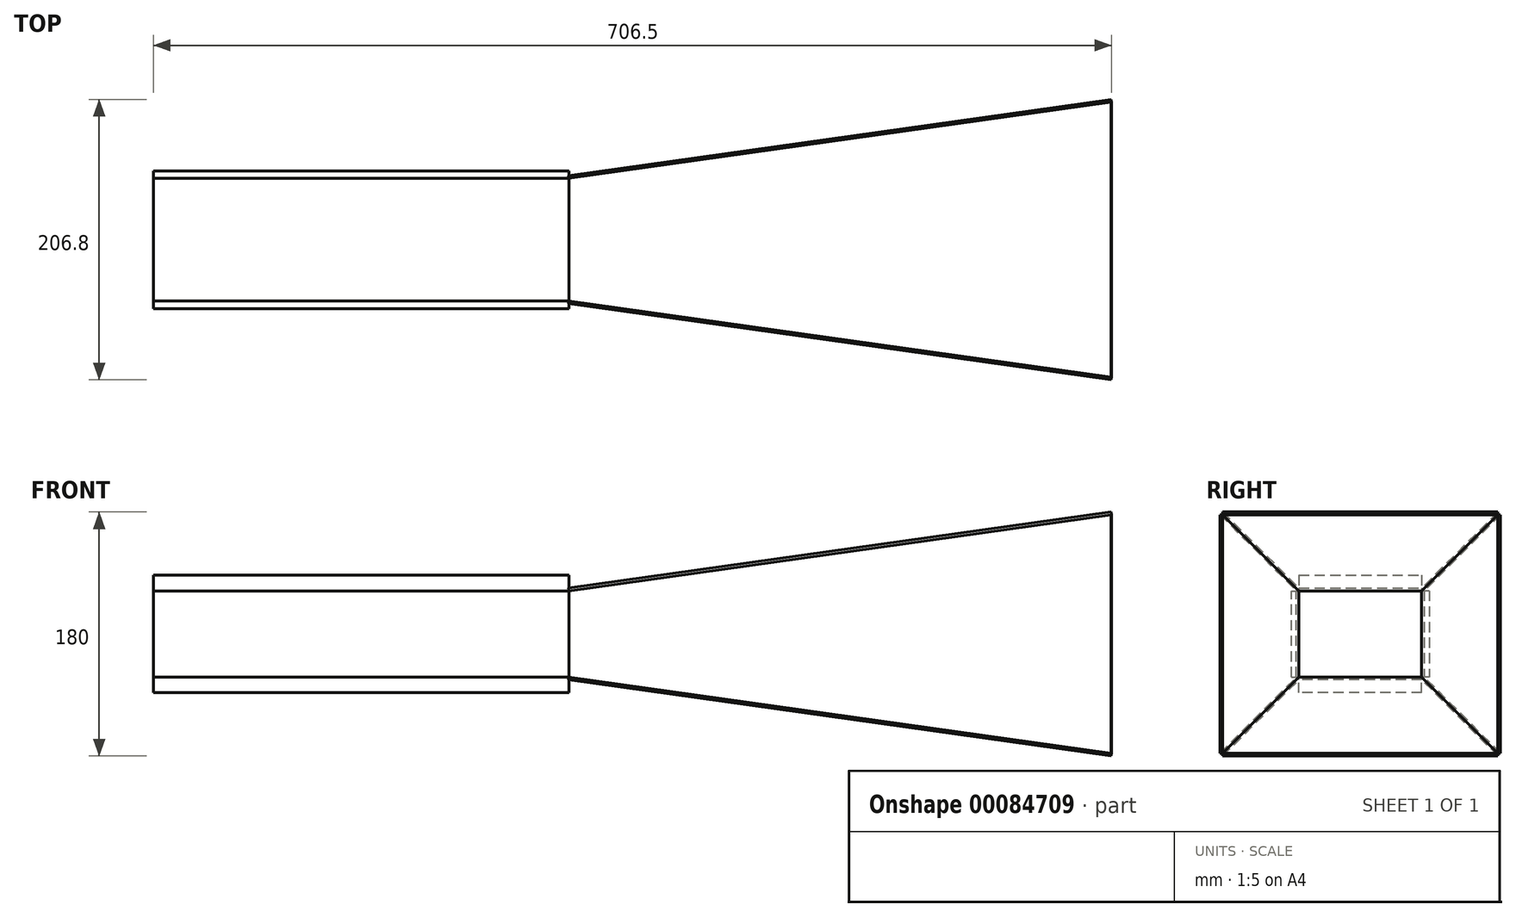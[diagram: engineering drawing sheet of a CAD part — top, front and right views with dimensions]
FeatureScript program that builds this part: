
annotation { "Feature Type Name" : "Feature", "Feature Type Description" : "" }
export const myFeature = defineFeature(function(context is Context, id is Id, definition is map)
    precondition{}
    {
        {
            var Q0;
            Q0=qCreatedBy(makeId("Right.planeOp"),FACE);
            var sketch = newSketch(context, id + "F0", { "sketchPlane" : qUnion([Q0])});
            skLineSegment(sketch, "E0", {"start": v(-45.2, 31.8) * mm, "end": v(45.2, 31.8) * mm});
            skLineSegment(sketch, "E1", {"start": v(45.2, 31.8) * mm, "end": v(45.2, -31.8) * mm});
            skLineSegment(sketch, "E2", {"start": v(45.2, -31.8) * mm, "end": v(-45.2, -31.8) * mm});
            skLineSegment(sketch, "E3", {"start": v(-45.2, -31.8) * mm, "end": v(-45.2, 31.8) * mm});
            skLineSegment(sketch, "E4", {"start": v(-45.2, 0) * mm, "end": v(45.2, 0) * mm, "construction": true});
            skSolve(sketch);
        }
        {
            var Q0;
            Q0=qCreatedBy(makeId("Right.planeOp"),FACE);
            cPlane(context, id + "F1", {"entities" : qUnion([Q0]), "cplaneType" : CPlaneType.OFFSET, "offset" : 400 * mm, "width" : 150 * mm, "height" : 150 * mm});
        }
        {
            var Q0;
            Q0=makeQuery(id+"F0.imprint","IMPRINT",FACE,{"disambiguationData":[TD([[makeQuery(id+"F0.imprint","IMPRINT",EDGE,{"derivedFrom":sQuery(id+"F0.wireOp",EDGE,"E0")}),-1.0]])]});
            var Q1;
            Q1=qCreatedBy(id+"F1.planeOp",FACE);
            extrude(context, id + "F2", {"entities" : qUnion([Q0]), "endBound" : BoundingType.UP_TO_SURFACE, "endBoundEntityFace" : qUnion([Q1]), "depth" : 25 * mm, "hasDraft" : true, "draftAngle" : 8 * degree});
        }
        {
            var Q0;
            Q0=makeQuery(id+"F2.opExtrude","SWEPT_FACE",FACE,{"disambiguationData":[OSD([sQuery(id+"F0.wireOp",EDGE,"E1")])]});
            extrude(context, id + "F3", {"entities" : qUnion([Q0]), "operationType" : NewBodyOperationType.ADD, "depth" : 2 * mm});
        }
        {
            var Q0;
            Q0=makeQuery(id+"F2.opExtrude","SWEPT_FACE",FACE,{"disambiguationData":[OSD([sQuery(id+"F0.wireOp",EDGE,"E0")])]});
            extrude(context, id + "F4", {"entities" : qUnion([Q0]), "operationType" : NewBodyOperationType.ADD, "depth" : 2 * mm});
        }
        {
            var Q0;
            Q0=makeQuery(id+"F2.opExtrude","SWEPT_FACE",FACE,{"disambiguationData":[OSD([sQuery(id+"F0.wireOp",EDGE,"E3")])]});
            extrude(context, id + "F5", {"entities" : qUnion([Q0]), "operationType" : NewBodyOperationType.ADD, "depth" : 2 * mm});
        }
        {
            var Q0;
            Q0=makeQuery(id+"F2.opExtrude","SWEPT_FACE",FACE,{"disambiguationData":[OSD([sQuery(id+"F0.wireOp",EDGE,"E2")])]});
            extrude(context, id + "F6", {"entities" : qUnion([Q0]), "operationType" : NewBodyOperationType.ADD, "depth" : 2 * mm});
        }
        {
            var Q0;
            Q0=makeQuery(id+"F2.opExtrude","CAP_FACE",FACE,{"disambiguationData":[OSD([sQuery(id+"F0.wireOp",EDGE,"E0"),sQuery(id+"F0.wireOp",EDGE,"E1"),sQuery(id+"F0.wireOp",EDGE,"E2"),sQuery(id+"F0.wireOp",EDGE,"E3")])],"isStart":false});
            extrude(context, id + "F7", {"entities" : qUnion([Q0]), "operationType" : NewBodyOperationType.REMOVE, "oppositeDirection" : true, "depth" : 400 * mm, "hasDraft" : true, "draftAngle" : 8 * degree, "draftPullDirection" : true});
        }
        {
            var Q0;
            Q0=makeQuery(id+"F0.imprint","IMPRINT",FACE,{"disambiguationData":[TD([[makeQuery(id+"F0.imprint","IMPRINT",EDGE,{"derivedFrom":sQuery(id+"F0.wireOp",EDGE,"E0")}),-1.0]])]});
            extrude(context, id + "F8", {"entities" : qUnion([Q0]), "oppositeDirection" : true, "depth" : 306.5 * mm});
        }
        {
            var Q0;
            Q0=makeQuery(id+"F8.opExtrude","SWEPT_FACE",FACE,{"disambiguationData":[OSD([sQuery(id+"F0.wireOp",EDGE,"E0")])]});
            extrude(context, id + "F9", {"entities" : qUnion([Q0]), "depth" : 11.6 * mm});
        }
        {
            var Q0;
            Q0=makeQuery(id+"F8.opExtrude","SWEPT_FACE",FACE,{"disambiguationData":[OSD([sQuery(id+"F0.wireOp",EDGE,"E3")])]});
            extrude(context, id + "F10", {"entities" : qUnion([Q0]), "depth" : 5.6 * mm});
        }
        {
            var Q0;
            Q0=makeQuery(id+"F8.opExtrude","SWEPT_FACE",FACE,{"disambiguationData":[OSD([sQuery(id+"F0.wireOp",EDGE,"E1")])]});
            extrude(context, id + "F11", {"entities" : qUnion([Q0]), "depth" : 5.6 * mm});
        }
        {
            var Q0;
            Q0=makeQuery(id+"F8.opExtrude","SWEPT_FACE",FACE,{"disambiguationData":[OSD([sQuery(id+"F0.wireOp",EDGE,"E2")])]});
            extrude(context, id + "F12", {"entities" : qUnion([Q0]), "depth" : 11.6 * mm});
        }
        {
            var Q0;
            Q0=makeQuery(id+"F0.imprint","IMPRINT",FACE,{"disambiguationData":[TD([[makeQuery(id+"F0.imprint","IMPRINT",EDGE,{"derivedFrom":sQuery(id+"F0.wireOp",EDGE,"E0")}),-1.0]])]});
            extrude(context, id + "F13", {"entities" : qUnion([Q0]), "operationType" : NewBodyOperationType.REMOVE, "oppositeDirection" : true, "depth" : 306.5 * mm});
        }
    });
